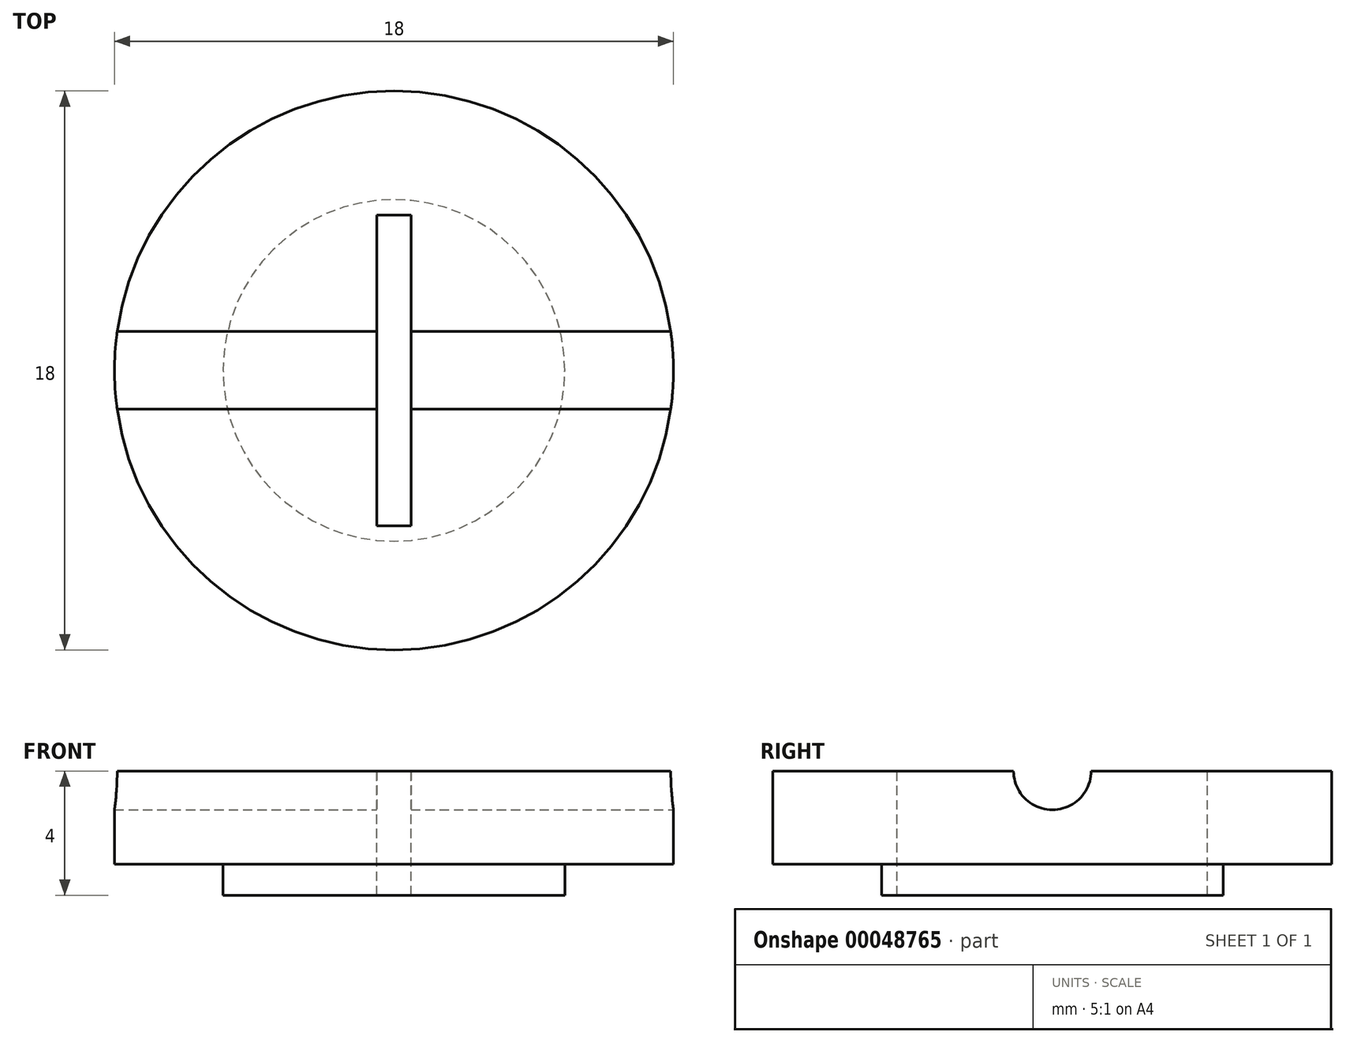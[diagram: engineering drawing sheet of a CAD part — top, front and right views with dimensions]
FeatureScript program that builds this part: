
annotation { "Feature Type Name" : "Feature", "Feature Type Description" : "" }
export const myFeature = defineFeature(function(context is Context, id is Id, definition is map)
    precondition{}
    {
        {
            var Q0;
            Q0=qCreatedBy(makeId("Top.planeOp"),FACE);
            var sketch = newSketch(context, id + "F0", { "sketchPlane" : qUnion([Q0])});
            skCircle(sketch, "E0", {"center": v(0, 0) * mm, "radius": 9 * mm});
            skSolve(sketch);
        }
        {
            var Q0;
            Q0=makeQuery(id+"F0.imprint","IMPRINT",FACE,{"disambiguationData":[TD([[makeQuery(id+"F0.imprint","IMPRINT",EDGE,{"derivedFrom":sQuery(id+"F0.wireOp",EDGE,"E0")}),1.0]])]});
            extrude(context, id + "F1", {"entities" : qUnion([Q0]), "oppositeDirection" : true, "depth" : 3 * mm});
        }
        {
            var Q0;
            Q0=makeQuery(id+"F1.opExtrude","CAP_FACE",FACE,{"disambiguationData":[OSD([sQuery(id+"F0.wireOp",EDGE,"E0")])],"isStart":false});
            var sketch = newSketch(context, id + "F2", { "sketchPlane" : qUnion([Q0])});
            skCircle(sketch, "E1", {"center": v(0, 0) * mm, "radius": 5.5 * mm});
            skSolve(sketch);
        }
        {
            var Q0;
            Q0=makeQuery(id+"F2.imprint","IMPRINT",FACE,{"disambiguationData":[TD([[makeQuery(id+"F2.imprint","IMPRINT",EDGE,{"derivedFrom":sQuery(id+"F2.wireOp",EDGE,"E1")}),1.0]])]});
            extrude(context, id + "F3", {"entities" : qUnion([Q0]), "operationType" : NewBodyOperationType.ADD, "depth" : 1 * mm});
        }
        {
            var Q0;
            Q0=qCreatedBy(makeId("Right.planeOp"),FACE);
            var sketch = newSketch(context, id + "F4", { "sketchPlane" : qUnion([Q0])});
            skPoint(sketch, "E2.middle", {"position": v(0, 0) * mm});
            skCircle(sketch, "E3", {"center": v(0, 0) * mm, "radius": 1.25 * mm});
            skSolve(sketch);
        }
        {
            var Q0;
            Q0=makeQuery(id+"F4.imprint","IMPRINT",FACE,{"disambiguationData":[TD([[makeQuery(id+"F4.imprint","IMPRINT",EDGE,{"derivedFrom":sQuery(id+"F4.wireOp",EDGE,"E3")}),1.0]])]});
            extrude(context, id + "F5", {"entities" : qUnion([Q0]), "operationType" : NewBodyOperationType.REMOVE, "oppositeDirection" : true, "depth" : 18 * mm, "symmetric" : true});
        }
        {
            var Q0;
            Q0=makeQuery(id+"F1.opExtrude","CAP_FACE",FACE,{"disambiguationData":[OSD([sQuery(id+"F0.wireOp",EDGE,"E0")])],"isStart":true});
            var sketch = newSketch(context, id + "F6", { "sketchPlane" : qUnion([Q0])});
            skLineSegment(sketch, "E4.bottom", {"start": v(0.55, -5) * mm, "end": v(-0.55, -5) * mm});
            skLineSegment(sketch, "E4.top", {"start": v(0.55, 5) * mm, "end": v(-0.55, 5) * mm});
            skLineSegment(sketch, "E4.left", {"start": v(0.55, -5) * mm, "end": v(0.55, 5) * mm});
            skLineSegment(sketch, "E4.right", {"start": v(-0.55, -5) * mm, "end": v(-0.55, 5) * mm});
            skPoint(sketch, "E4.middle", {"position": v(0, 0) * mm});
            skSolve(sketch);
        }
        {
            var Q0;
            Q0=makeQuery(id+"F6.imprint","IMPRINT",FACE,{"disambiguationData":[TD([[makeQuery(id+"F6.imprint","IMPRINT",EDGE,{"derivedFrom":sQuery(id+"F6.wireOp",EDGE,"E4.bottom")}),-1.0]])]});
            var Q1;
            {var subQ0=sQuery(id+"F6.wireOp",EDGE,"E4.left");var subQ1=makeQuery(id+"F5.boolean.opBoolean","COPY",EDGE,{"derivedFrom":makeQuery(id+"F5.opExtrude","CAP_EDGE",EDGE,{"disambiguationData":[OSD([sQuery(id+"F4.wireOp",EDGE,"E2.bottom")])],"isStart":true})});var subQ2=makeQuery(id+"F6.imprint","INTERSECT",VERTEX,{"derivedFrom":[subQ1,subQ0]});Q1=makeQuery(id+"F6.imprint","IMPRINT",FACE,{"disambiguationData":[TD([[makeQuery(id+"F6.imprint","IMPRINT",EDGE,{"disambiguationData":[TD([[subQ2,-1.0]])],"derivedFrom":subQ0}),1.0]])]});}
            var Q2;
            {var subQ0=sQuery(id+"F6.wireOp",EDGE,"E4.top");Q2=makeQuery(id+"F6.imprint","IMPRINT",FACE,{"disambiguationData":[TD([[makeQuery(id+"F6.imprint","IMPRINT",EDGE,{"derivedFrom":subQ0}),1.0]])]});}
            extrude(context, id + "F7", {"entities" : qUnion([Q0, Q1, Q2]), "operationType" : NewBodyOperationType.REMOVE, "endBound" : BoundingType.THROUGH_ALL, "oppositeDirection" : true, "depth" : 25 * mm});
        }
    });
